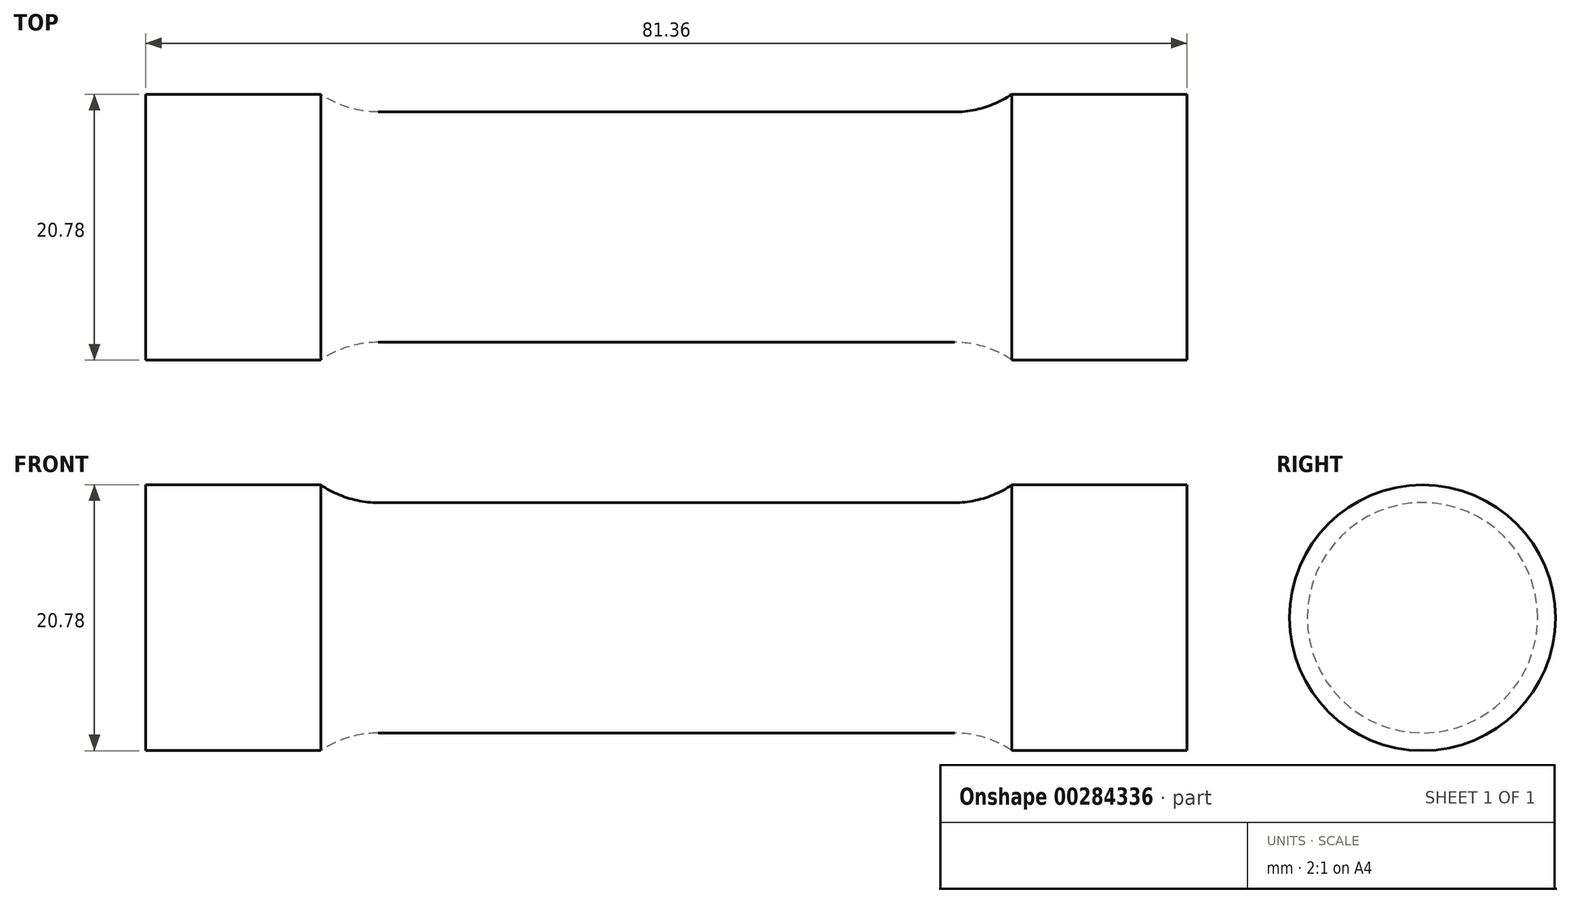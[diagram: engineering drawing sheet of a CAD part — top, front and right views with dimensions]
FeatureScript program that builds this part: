
annotation { "Feature Type Name" : "Feature", "Feature Type Description" : "" }
export const myFeature = defineFeature(function(context is Context, id is Id, definition is map)
    precondition{}
    {
        {
            var Q0;
            Q0=qCreatedBy(makeId("Front.planeOp"),FACE);
            var sketch = newSketch(context, id + "F0", { "sketchPlane" : qUnion([Q0])});
            skLineSegment(sketch, "E0", {"start": v(0, 9) * mm, "end": v(22.5, 9) * mm});
            skArc(sketch, "E1", {"start": v(22.5, 9) * mm, "mid": v(24.85, 9.35) * mm, "end": v(27, 10.39) * mm});
            skLineSegment(sketch, "E2", {"start": v(27, 10.39) * mm, "end": v(40.68, 10.39) * mm});
            skLineSegment(sketch, "E3", {"start": v(40.68, 10.39) * mm, "end": v(40.68, 0) * mm});
            skLineSegment(sketch, "E4.MirrorCS", {"start": v(-40.68, 10.39) * mm, "end": v(-40.68, 0) * mm});
            skLineSegment(sketch, "E5.MirrorCS", {"start": v(0, 9) * mm, "end": v(-22.5, 9) * mm});
            skLineSegment(sketch, "E6.MirrorCS", {"start": v(-27, 10.39) * mm, "end": v(-40.68, 10.39) * mm});
            skArc(sketch, "E7.MirrorCS", {"start": v(-22.5, 9) * mm, "mid": v(-24.85, 9.35) * mm, "end": v(-27, 10.39) * mm});
            skLineSegment(sketch, "E8", {"start": v(-40.68, 0) * mm, "end": v(40.68, 0) * mm});
            skSolve(sketch);
        }
        {
            var Q0;
            Q0 = qSketchRegion(id + "F0", true);
            var Q1;
            Q1=sQuery(id+"F0.wireOp",EDGE,"E8");
            revolve(context, id + "F1", {"entities" : qUnion([Q0]), "axis" : qUnion([Q1]), "revolveType" : RevolveType.FULL});
        }
    });
